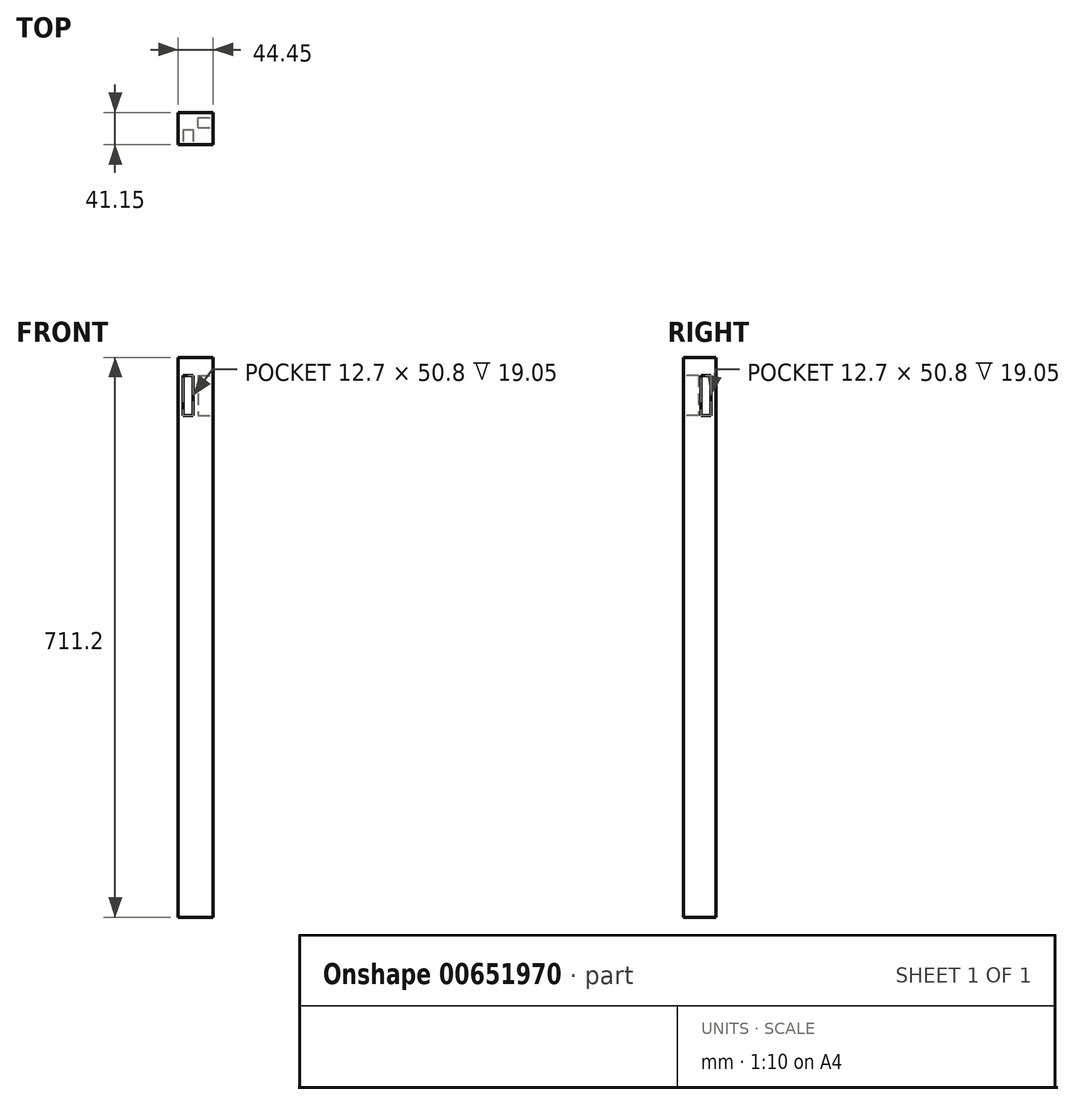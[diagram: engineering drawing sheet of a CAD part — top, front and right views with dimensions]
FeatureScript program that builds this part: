
annotation { "Feature Type Name" : "Feature", "Feature Type Description" : "" }
export const myFeature = defineFeature(function(context is Context, id is Id, definition is map)
    precondition{}
    {
        {
            var Q0;
            Q0=qCreatedBy(makeId("Top.planeOp"),FACE);
            var sketch = newSketch(context, id + "F0", { "sketchPlane" : qUnion([Q0])});
            skLineSegment(sketch, "E0.bottom", {"start": v(-27.26, 31.94) * mm, "end": v(17.2, 31.94) * mm});
            skLineSegment(sketch, "E0.top", {"start": v(-27.26, -9.2) * mm, "end": v(17.2, -9.2) * mm});
            skLineSegment(sketch, "E0.left", {"start": v(-27.26, 31.94) * mm, "end": v(-27.26, -9.2) * mm});
            skLineSegment(sketch, "E0.right", {"start": v(17.2, 31.94) * mm, "end": v(17.2, -9.2) * mm});
            skSolve(sketch);
        }
        {
            var Q0;
            Q0=makeQuery(id+"F0.imprint","IMPRINT",FACE,{"disambiguationData":[TD([[makeQuery(id+"F0.imprint","IMPRINT",EDGE,{"derivedFrom":sQuery(id+"F0.wireOp",EDGE,"E0.bottom")}),-1.0]])]});
            extrude(context, id + "F1", {"entities" : qUnion([Q0]), "endBound" : BoundingType.SYMMETRIC, "depth" : 711.2 * mm, "offsetDistance" : 25.4 * mm});
        }
        {
            var Q0;
            Q0=makeQuery(id+"F1.opExtrude","SWEPT_FACE",FACE,{"disambiguationData":[OSD([sQuery(id+"F0.wireOp",EDGE,"E0.top")])]});
            var sketch = newSketch(context, id + "F2", { "sketchPlane" : qUnion([Q0])});
            skLineSegment(sketch, "E1.bottom", {"start": v(-20.9, 332.74) * mm, "end": v(-8.2, 332.74) * mm});
            skLineSegment(sketch, "E1.top", {"start": v(-20.9, 281.94) * mm, "end": v(-8.2, 281.94) * mm});
            skLineSegment(sketch, "E1.left", {"start": v(-20.9, 332.74) * mm, "end": v(-20.9, 281.94) * mm});
            skLineSegment(sketch, "E1.right", {"start": v(-8.2, 332.74) * mm, "end": v(-8.2, 281.94) * mm});
            skSolve(sketch);
        }
        {
            var Q0;
            Q0 = qSketchRegion(id + "F2", true);
            extrude(context, id + "F3", {"entities" : qUnion([Q0]), "operationType" : NewBodyOperationType.REMOVE, "oppositeDirection" : true, "depth" : 19.05 * mm, "offsetDistance" : 25.4 * mm});
        }
        {
            var Q0;
            Q0=makeQuery(id+"F1.opExtrude","SWEPT_FACE",FACE,{"disambiguationData":[OSD([sQuery(id+"F0.wireOp",EDGE,"E0.right")])]});
            var sketch = newSketch(context, id + "F4", { "sketchPlane" : qUnion([Q0])});
            skLineSegment(sketch, "E2.bottom", {"start": v(12.9, 332.74) * mm, "end": v(25.6, 332.74) * mm});
            skLineSegment(sketch, "E2.top", {"start": v(12.9, 281.94) * mm, "end": v(25.6, 281.94) * mm});
            skLineSegment(sketch, "E2.left", {"start": v(12.9, 332.74) * mm, "end": v(12.9, 281.94) * mm});
            skLineSegment(sketch, "E2.right", {"start": v(25.6, 332.74) * mm, "end": v(25.6, 281.94) * mm});
            skSolve(sketch);
        }
        {
            var Q0;
            Q0 = qSketchRegion(id + "F4", true);
            extrude(context, id + "F5", {"entities" : qUnion([Q0]), "operationType" : NewBodyOperationType.REMOVE, "oppositeDirection" : true, "depth" : 19.05 * mm, "offsetDistance" : 25.4 * mm});
        }
        {
            var Q0;
            Q0=makeQuery(id+"F1.opExtrude","SWEPT_BODY",BODY,{"disambiguationData":[OSD([sQuery(id+"F0.wireOp",EDGE,"E0.bottom"),sQuery(id+"F0.wireOp",EDGE,"E0.top"),sQuery(id+"F0.wireOp",EDGE,"E0.left"),sQuery(id+"F0.wireOp",EDGE,"E0.right")])]});
            transform(context, id + "F6", {"entities" : qUnion([Q0]), "transformType" : TransformType.TRANSLATION_3D, "dx" : 0 * mm, "dy" : 0 * mm, "dz" : 0 * mm, "makeCopy" : true});
        }
        {
            var Q0;
            Q0=makeQuery(id+"F6.opPattern","COPY",BODY,{"derivedFrom":makeQuery(id+"F1.opExtrude","SWEPT_BODY",BODY,{"disambiguationData":[OSD([sQuery(id+"F0.wireOp",EDGE,"E0.bottom"),sQuery(id+"F0.wireOp",EDGE,"E0.top"),sQuery(id+"F0.wireOp",EDGE,"E0.left"),sQuery(id+"F0.wireOp",EDGE,"E0.right")])]}),"instanceName":"1"});
            deleteBodies(context, id + "F7", {"entities" : qUnion([Q0])});
        }
        {
            var Q0;
            Q0=makeQuery(id+"F1.opExtrude","SWEPT_BODY",BODY,{"disambiguationData":[OSD([sQuery(id+"F0.wireOp",EDGE,"E0.bottom"),sQuery(id+"F0.wireOp",EDGE,"E0.top"),sQuery(id+"F0.wireOp",EDGE,"E0.left"),sQuery(id+"F0.wireOp",EDGE,"E0.right")])]});
            transform(context, id + "F8", {"entities" : qUnion([Q0]), "transformType" : TransformType.TRANSLATION_3D, "dx" : 0 * mm, "dy" : 0 * mm, "dz" : 0 * mm, "makeCopy" : true});
        }
        {
            var Q0;
            Q0=makeQuery(id+"F8.opPattern","COPY",BODY,{"derivedFrom":makeQuery(id+"F1.opExtrude","SWEPT_BODY",BODY,{"disambiguationData":[OSD([sQuery(id+"F0.wireOp",EDGE,"E0.bottom"),sQuery(id+"F0.wireOp",EDGE,"E0.top"),sQuery(id+"F0.wireOp",EDGE,"E0.left"),sQuery(id+"F0.wireOp",EDGE,"E0.right")])]}),"instanceName":"1"});
            deleteBodies(context, id + "F9", {"entities" : qUnion([Q0])});
        }
        {
            var Q0;
            Q0=makeQuery(id+"F1.opExtrude","SWEPT_BODY",BODY,{"disambiguationData":[OSD([sQuery(id+"F0.wireOp",EDGE,"E0.bottom"),sQuery(id+"F0.wireOp",EDGE,"E0.top"),sQuery(id+"F0.wireOp",EDGE,"E0.left"),sQuery(id+"F0.wireOp",EDGE,"E0.right")])]});
            transform(context, id + "F10", {"entities" : qUnion([Q0]), "transformType" : TransformType.TRANSLATION_3D, "dx" : 0 * mm, "dy" : 0 * mm, "dz" : 0 * mm, "makeCopy" : true});
        }
        {
            var Q0;
            Q0=makeQuery(id+"F10.opPattern","COPY",BODY,{"derivedFrom":makeQuery(id+"F1.opExtrude","SWEPT_BODY",BODY,{"disambiguationData":[OSD([sQuery(id+"F0.wireOp",EDGE,"E0.bottom"),sQuery(id+"F0.wireOp",EDGE,"E0.top"),sQuery(id+"F0.wireOp",EDGE,"E0.left"),sQuery(id+"F0.wireOp",EDGE,"E0.right")])]}),"instanceName":"1"});
            deleteBodies(context, id + "F11", {"entities" : qUnion([Q0])});
        }
    });
